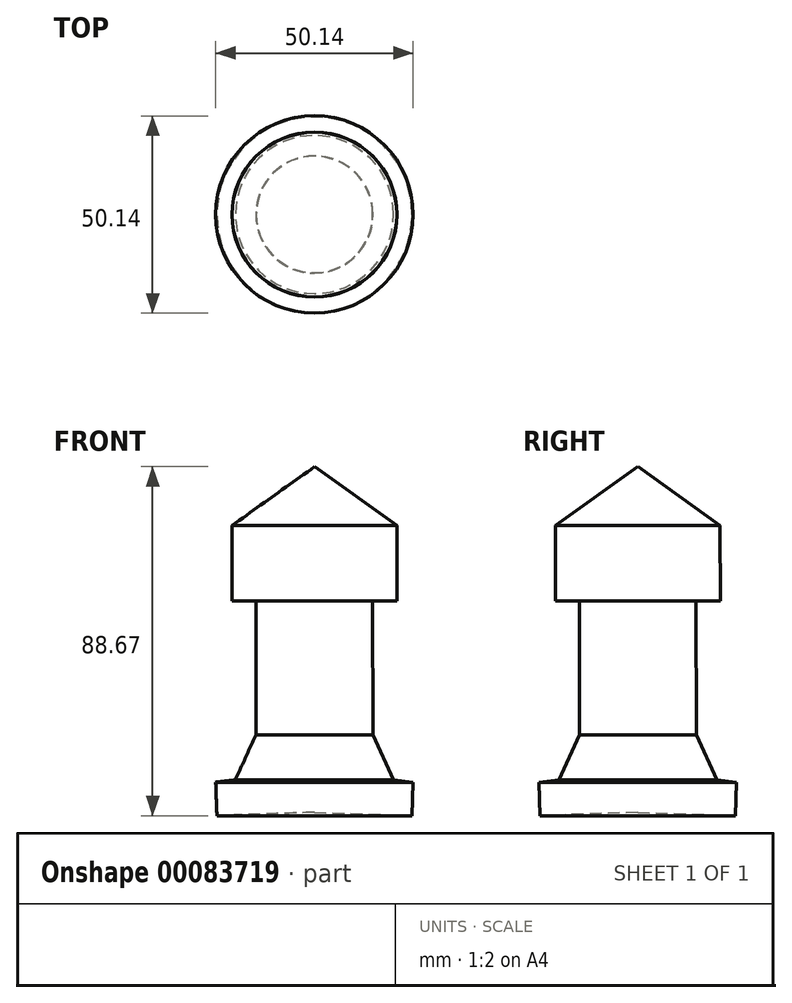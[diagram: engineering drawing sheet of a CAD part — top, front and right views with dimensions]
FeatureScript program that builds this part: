
annotation { "Feature Type Name" : "Feature", "Feature Type Description" : "" }
export const myFeature = defineFeature(function(context is Context, id is Id, definition is map)
    precondition{}
    {
        {
            var Q0;
            Q0=qCreatedBy(makeId("Front.planeOp"),FACE);
            var sketch = newSketch(context, id + "F0", { "sketchPlane" : qUnion([Q0])});
            skLineSegment(sketch, "E0", {"start": v(0, 49.76) * mm, "end": v(-20.92, 34.82) * mm});
            skLineSegment(sketch, "E1", {"start": v(-20.92, 34.82) * mm, "end": v(0, 34.82) * mm});
            skLineSegment(sketch, "E2", {"start": v(0, 49.76) * mm, "end": v(0, 34.82) * mm});
            skLineSegment(sketch, "E3", {"start": v(-20.92, 34.82) * mm, "end": v(-20.96, 15.69) * mm});
            skLineSegment(sketch, "E4", {"start": v(-20.96, 15.69) * mm, "end": v(0, 15.64) * mm});
            skLineSegment(sketch, "E5", {"start": v(0, 15.64) * mm, "end": v(0, 34.82) * mm});
            skLineSegment(sketch, "E6", {"start": v(-14.8, 15.67) * mm, "end": v(-14.87, -18.36) * mm});
            skLineSegment(sketch, "E7", {"start": v(-14.87, -18.36) * mm, "end": v(-20.08, -29.81) * mm});
            skLineSegment(sketch, "E8", {"start": v(-20.08, -29.81) * mm, "end": v(-25.07, -30.4) * mm});
            skLineSegment(sketch, "E9", {"start": v(-25.07, -30.4) * mm, "end": v(-24.78, -38.91) * mm});
            skLineSegment(sketch, "E10", {"start": v(-24.78, -38.91) * mm, "end": v(0, -38.06) * mm});
            skLineSegment(sketch, "E11", {"start": v(0, -38.06) * mm, "end": v(0, 15.64) * mm});
            skSolve(sketch);
        }
        {
            var Q0;
            Q0 = qSketchRegion(id + "F0", true);
            var Q1;
            Q1=sQuery(id+"F0.wireOp",EDGE,"E11");
            revolve(context, id + "F1", {"entities" : qUnion([Q0]), "axis" : qUnion([Q1]), "revolveType" : RevolveType.FULL});
        }
    });
